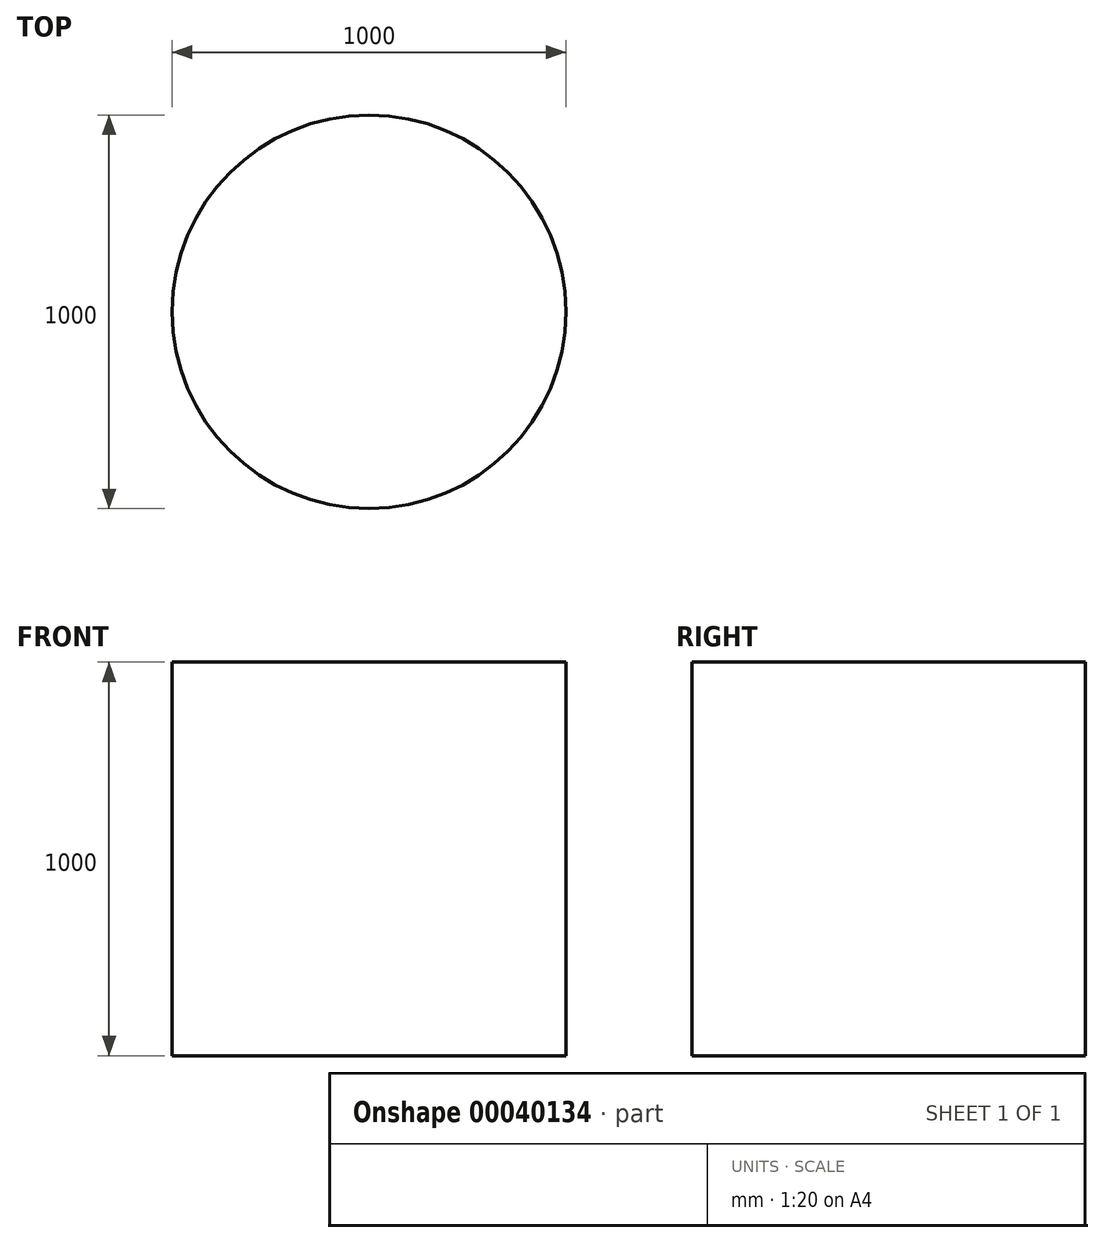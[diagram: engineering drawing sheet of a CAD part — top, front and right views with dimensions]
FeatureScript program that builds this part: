
annotation { "Feature Type Name" : "Feature", "Feature Type Description" : "" }
export const myFeature = defineFeature(function(context is Context, id is Id, definition is map)
    precondition{}
    {
        {
            var Q0;
            Q0=qCreatedBy(makeId("Top.planeOp"),FACE);
            var sketch = newSketch(context, id + "F0", { "sketchPlane" : qUnion([Q0])});
            skCircle(sketch, "E0", {"center": v(-55.66, 56.3) * mm, "radius": 500 * mm});
            skSolve(sketch);
        }
        {
            var Q0;
            Q0=makeQuery(id+"F0.imprint","IMPRINT",FACE,{"disambiguationData":[TD([[makeQuery(id+"F0.imprint","IMPRINT",EDGE,{"derivedFrom":sQuery(id+"F0.wireOp",EDGE,"E0")}),1.0]])]});
            extrude(context, id + "F1", {"entities" : qUnion([Q0]), "depth" : 1000 * mm});
        }
    });
